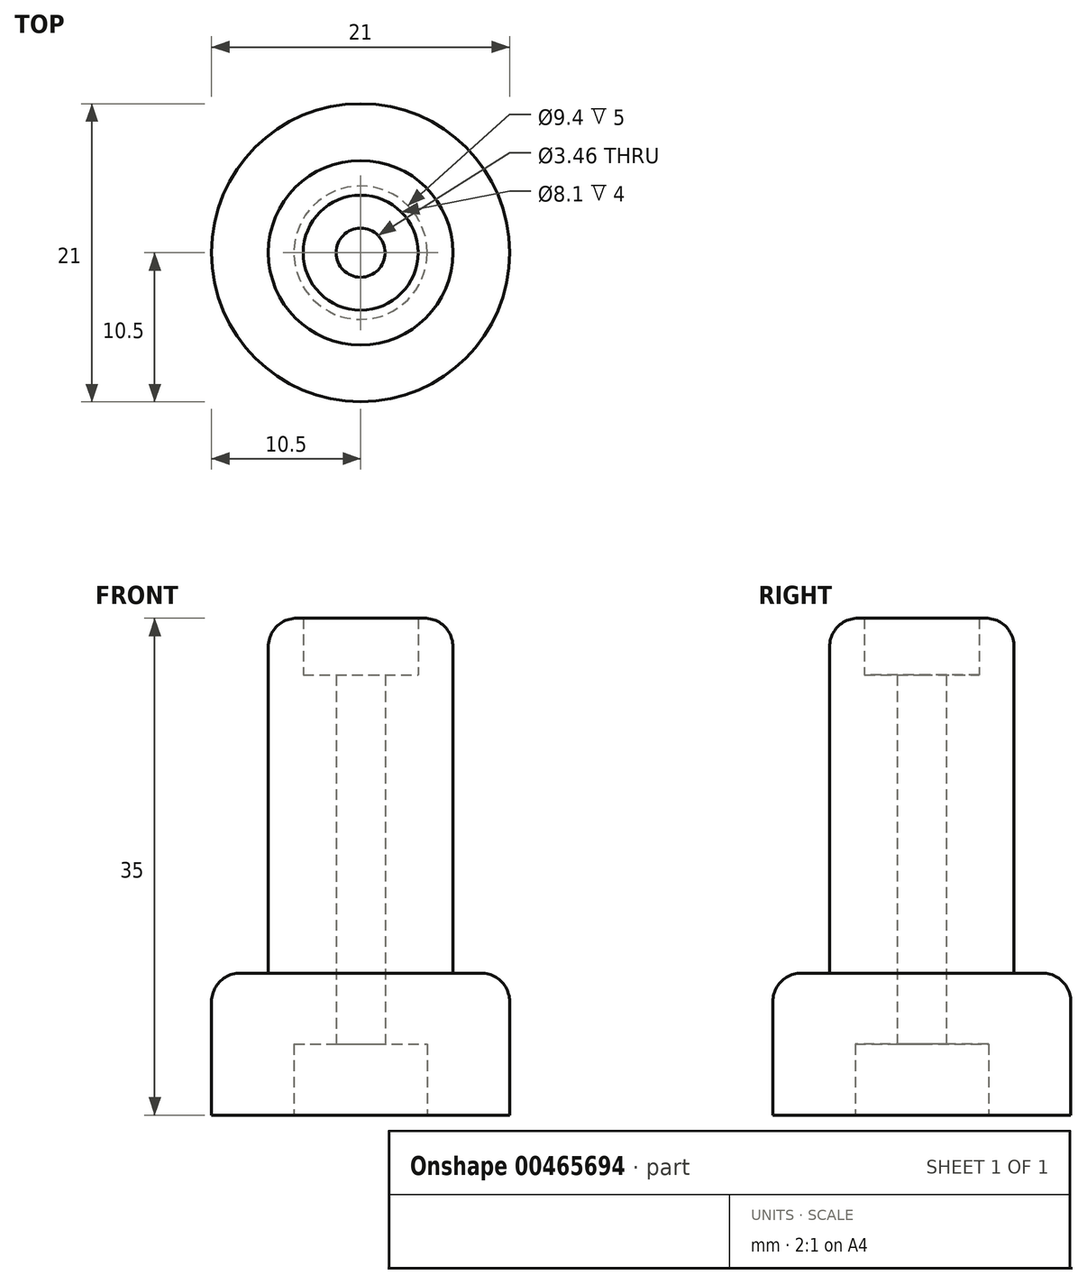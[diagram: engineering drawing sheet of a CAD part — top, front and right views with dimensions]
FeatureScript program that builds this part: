
annotation { "Feature Type Name" : "Feature", "Feature Type Description" : "" }
export const myFeature = defineFeature(function(context is Context, id is Id, definition is map)
    precondition{}
    {
        {
            var Q0;
            Q0=qCreatedBy(makeId("Front.planeOp"),FACE);
            var sketch = newSketch(context, id + "F0", { "sketchPlane" : qUnion([Q0])});
            skLineSegment(sketch, "E0", {"start": v(-4.7, 0) * mm, "end": v(-10.5, 0) * mm});
            skLineSegment(sketch, "E1", {"start": v(-10.5, 0) * mm, "end": v(-10.5, 10) * mm});
            skLineSegment(sketch, "E2", {"start": v(-10.5, 10) * mm, "end": v(-6.5, 10) * mm});
            skLineSegment(sketch, "E3", {"start": v(-4.7, 0) * mm, "end": v(-4.7, 5) * mm});
            skLineSegment(sketch, "E4", {"start": v(-4.7, 5) * mm, "end": v(-1.73, 5) * mm});
            skLineSegment(sketch, "E5", {"start": v(-6.5, 35) * mm, "end": v(-4.05, 35) * mm});
            skLineSegment(sketch, "E6", {"start": v(-4.05, 35) * mm, "end": v(-4.05, 31) * mm});
            skLineSegment(sketch, "E7", {"start": v(-4.05, 31) * mm, "end": v(-1.73, 31) * mm});
            skLineSegment(sketch, "E8", {"start": v(0, 0) * mm, "end": v(0, 34) * mm});
            skLineSegment(sketch, "E9", {"start": v(-6.5, 10) * mm, "end": v(-6.5, 35) * mm});
            skLineSegment(sketch, "E10", {"start": v(-1.73, 31) * mm, "end": v(-1.73, 5) * mm});
            skSolve(sketch);
        }
        {
            var Q0;
            Q0=makeQuery(id+"F0.imprint","IMPRINT",FACE,{"disambiguationData":[TD([[makeQuery(id+"F0.imprint","IMPRINT",EDGE,{"derivedFrom":sQuery(id+"F0.wireOp",EDGE,"E0")}),-1.0]])]});
            var Q1;
            Q1=sQuery(id+"F0.wireOp",EDGE,"E8");
            revolve(context, id + "F1", {"entities" : qUnion([Q0]), "axis" : qUnion([Q1]), "revolveType" : RevolveType.FULL});
        }
        {
            var Q0;
            Q0=makeQuery(id+"F1.opRevolve","SWEPT_EDGE",EDGE,{"disambiguationData":[OSD([sQuery(id+"F0.wireOp",EDGE,"E1"),sQuery(id+"F0.wireOp",EDGE,"E2")])]});
            var Q1;
            Q1=makeQuery(id+"F1.opRevolve","SWEPT_EDGE",EDGE,{"disambiguationData":[OSD([sQuery(id+"F0.wireOp",EDGE,"E5"),sQuery(id+"F0.wireOp",EDGE,"E9")])]});
            fillet(context, id + "F2", {"entities" : qUnion([Q0, Q1]), "radius" : 2 * mm, "tangentPropagation" : true, "allowEdgeOverflow" : false});
        }
    });
